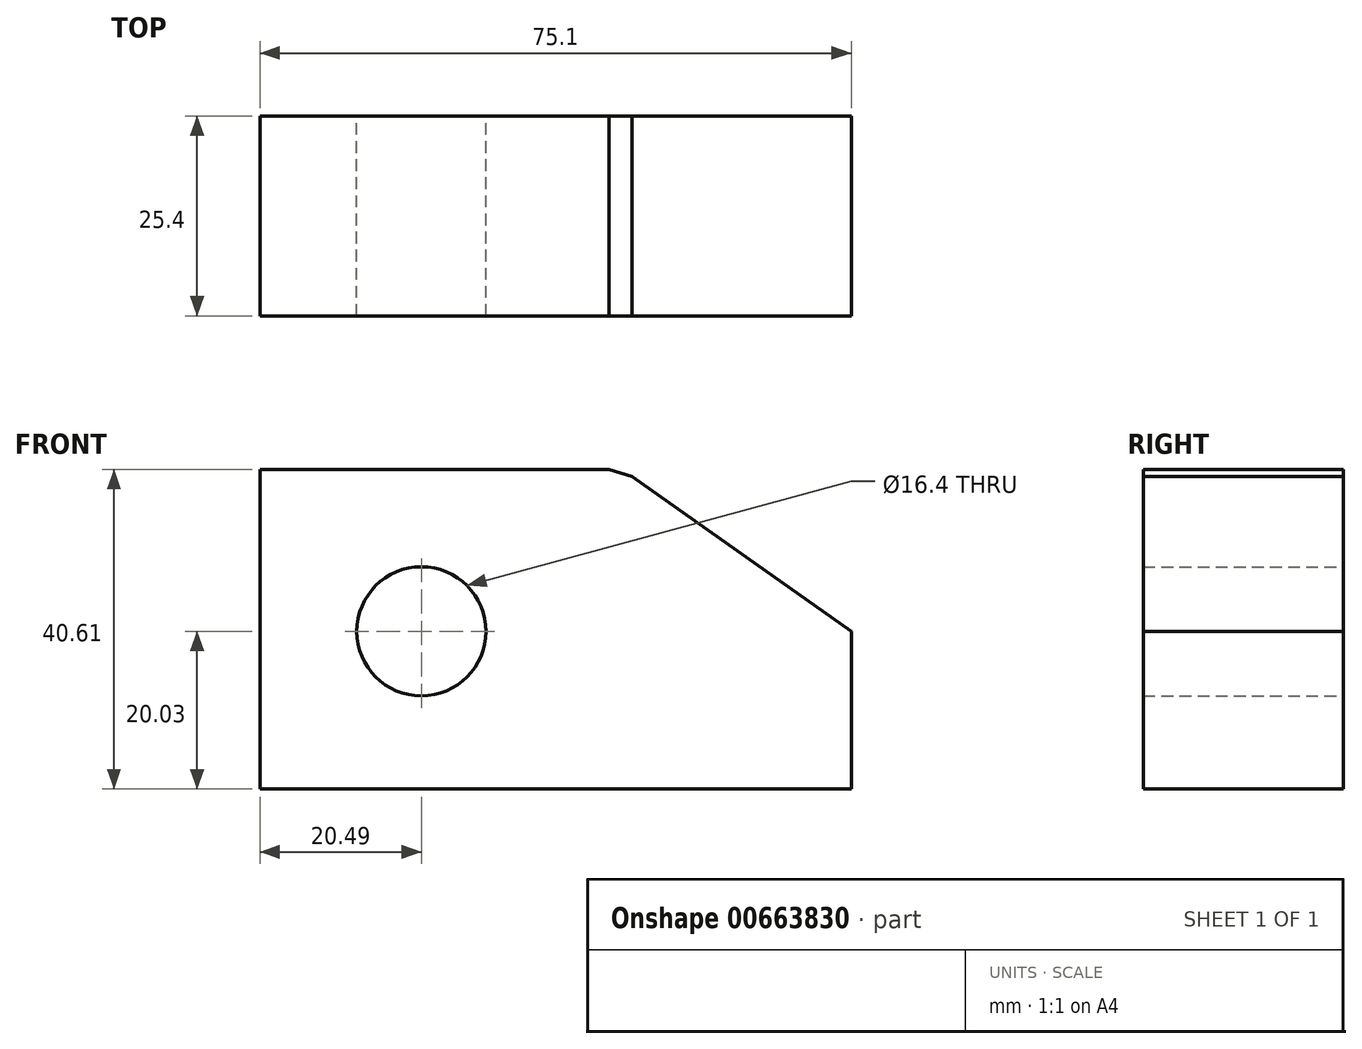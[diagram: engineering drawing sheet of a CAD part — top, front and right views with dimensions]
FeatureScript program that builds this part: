
annotation { "Feature Type Name" : "Feature", "Feature Type Description" : "" }
export const myFeature = defineFeature(function(context is Context, id is Id, definition is map)
    precondition{}
    {
        {
            var Q0;
            Q0=qCreatedBy(makeId("Front.planeOp"),FACE);
            var sketch = newSketch(context, id + "F0", { "sketchPlane" : qUnion([Q0])});
            skLineSegment(sketch, "E0", {"start": v(-20.49, 20.58) * mm, "end": v(25.46, 20.58) * mm});
            skLineSegment(sketch, "E1", {"start": v(25.46, 20.58) * mm, "end": v(54.6, 0) * mm});
            skLineSegment(sketch, "E2", {"start": v(54.6, 0) * mm, "end": v(54.6, -20.03) * mm});
            skLineSegment(sketch, "E3", {"start": v(54.6, -20.03) * mm, "end": v(-20.49, -20.03) * mm});
            skLineSegment(sketch, "E4", {"start": v(-20.49, -20.03) * mm, "end": v(-20.49, 20.58) * mm});
            skCircle(sketch, "E5", {"center": v(0, 0) * mm, "radius": 8.2 * mm});
            skSolve(sketch);
        }
        {
            var Q0;
            Q0=makeQuery(id+"F0.imprint","IMPRINT",FACE,{"disambiguationData":[TD([[makeQuery(id+"F0.imprint","IMPRINT",EDGE,{"derivedFrom":sQuery(id+"F0.wireOp",EDGE,"E0")}),-1.0]])]});
            extrude(context, id + "F1", {"entities" : qUnion([Q0]), "depth" : 25.4 * mm, "offsetDistance" : 25.4 * mm});
        }
        {
            var Q0;
            Q0=makeQuery(id+"F1.opExtrude","SWEPT_EDGE",EDGE,{"disambiguationData":[OSD([sQuery(id+"F0.wireOp",EDGE,"E0"),sQuery(id+"F0.wireOp",EDGE,"E1")])]});
            chamfer(context, id + "F2", {"entities" : qUnion([Q0]), "width" : 5.08 * mm, "tangentPropagation" : true});
        }
    });
